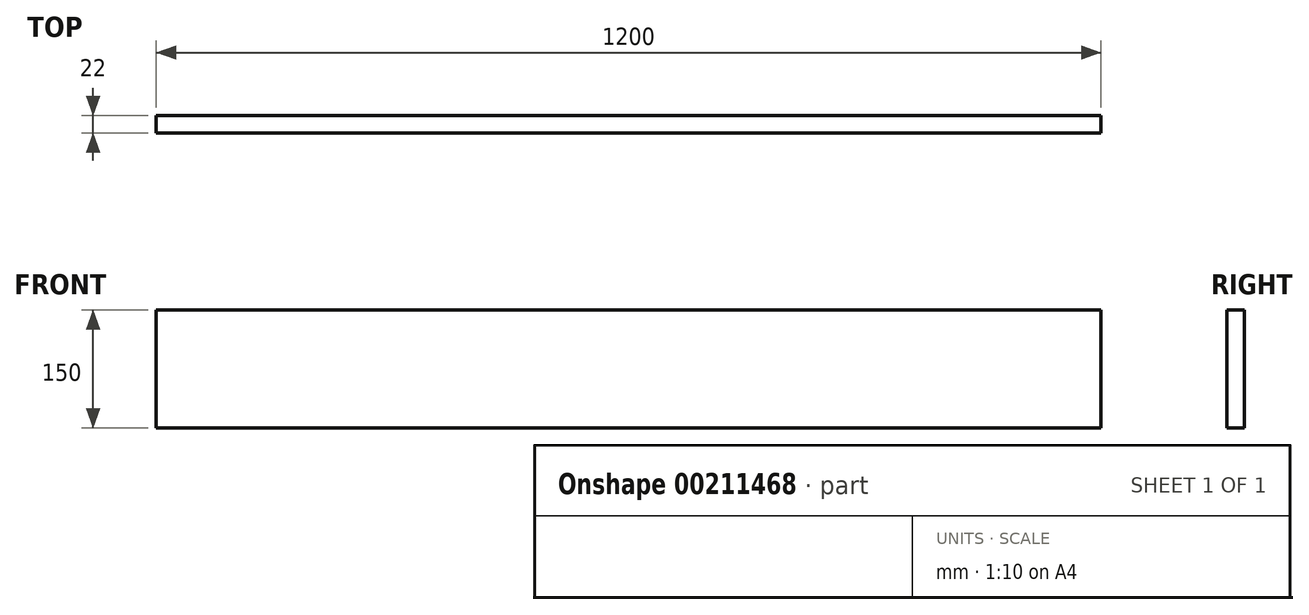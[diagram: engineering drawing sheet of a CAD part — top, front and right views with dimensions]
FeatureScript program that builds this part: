
annotation { "Feature Type Name" : "Feature", "Feature Type Description" : "" }
export const myFeature = defineFeature(function(context is Context, id is Id, definition is map)
    precondition{}
    {
        {
            var Q0;
            Q0=qCreatedBy(makeId("Front.planeOp"),FACE);
            var sketch = newSketch(context, id + "F0", { "sketchPlane" : qUnion([Q0])});
            skLineSegment(sketch, "E0.bottom", {"start": v(-600, 75) * mm, "end": v(600, 75) * mm});
            skLineSegment(sketch, "E0.top", {"start": v(-600, -75) * mm, "end": v(600, -75) * mm});
            skLineSegment(sketch, "E0.left", {"start": v(-600, 75) * mm, "end": v(-600, -75) * mm});
            skLineSegment(sketch, "E0.right", {"start": v(600, 75) * mm, "end": v(600, -75) * mm});
            skSolve(sketch);
        }
        {
            var Q0;
            Q0 = qSketchRegion(id + "F0", true);
            extrude(context, id + "F1", {"entities" : qUnion([Q0]), "depth" : 22 * mm});
        }
    });
